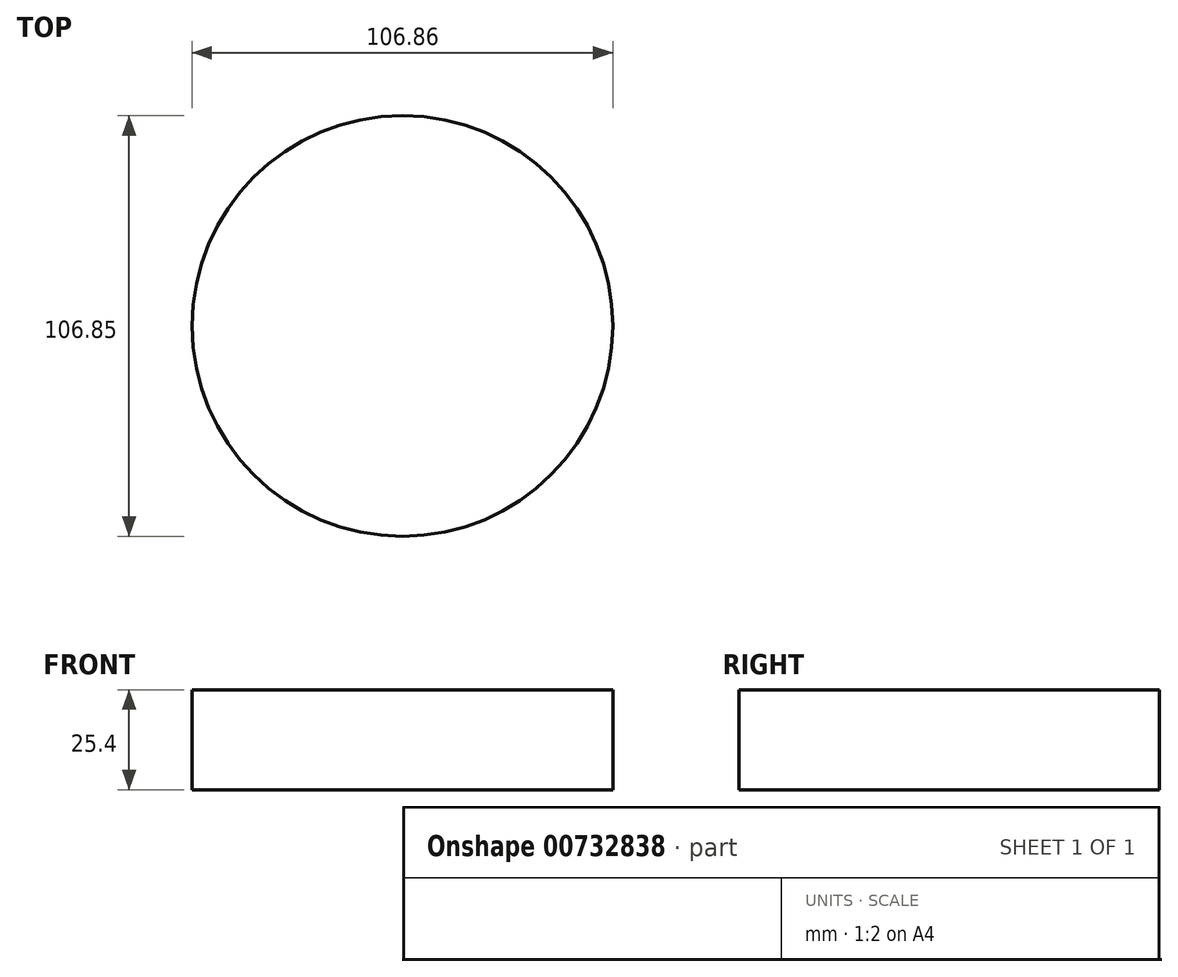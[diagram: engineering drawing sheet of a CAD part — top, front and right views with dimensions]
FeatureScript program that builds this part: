
annotation { "Feature Type Name" : "Feature", "Feature Type Description" : "" }
export const myFeature = defineFeature(function(context is Context, id is Id, definition is map)
    precondition{}
    {
        {
            var Q0;
            Q0=qCreatedBy(makeId("Top.planeOp"),FACE);
            var sketch = newSketch(context, id + "F0", { "sketchPlane" : qUnion([Q0])});
            skCircle(sketch, "E0", {"center": v(0, 0) * mm, "radius": 36.13 * mm});
            skCircle(sketch, "E1", {"center": v(11.9, 14) * mm, "radius": 53.43 * mm});
            skSolve(sketch);
        }
        {
            var Q0;
            {var subQ0=sQuery(id+"F0.wireOp",EDGE,"E1");var subQ1=sQuery(id+"F0.wireOp",EDGE,"E0");var subQ2=makeQuery(id+"F0.imprint","INTERSECT",VERTEX,{"disambiguationData":[OD(0.0)],"derivedFrom":[subQ1,subQ0]});Q0=makeQuery(id+"F0.imprint","IMPRINT",FACE,{"disambiguationData":[TD([[makeQuery(id+"F0.imprint","IMPRINT",EDGE,{"disambiguationData":[TD([[subQ2,1.0]])],"derivedFrom":subQ1}),1.0]])]});}
            var Q1;
            {var subQ0=sQuery(id+"F0.wireOp",EDGE,"E1");var subQ1=sQuery(id+"F0.wireOp",EDGE,"E0");var subQ2=makeQuery(id+"F0.imprint","INTERSECT",VERTEX,{"disambiguationData":[OD(0.0)],"derivedFrom":[subQ1,subQ0]});Q1=makeQuery(id+"F0.imprint","IMPRINT",FACE,{"disambiguationData":[TD([[makeQuery(id+"F0.imprint","IMPRINT",EDGE,{"disambiguationData":[TD([[subQ2,1.0]])],"derivedFrom":subQ1}),-1.0]])]});}
            extrude(context, id + "F1", {"entities" : qUnion([Q0, Q1]), "depth" : 25.4 * mm, "offsetDistance" : 25.4 * mm});
        }
    });
